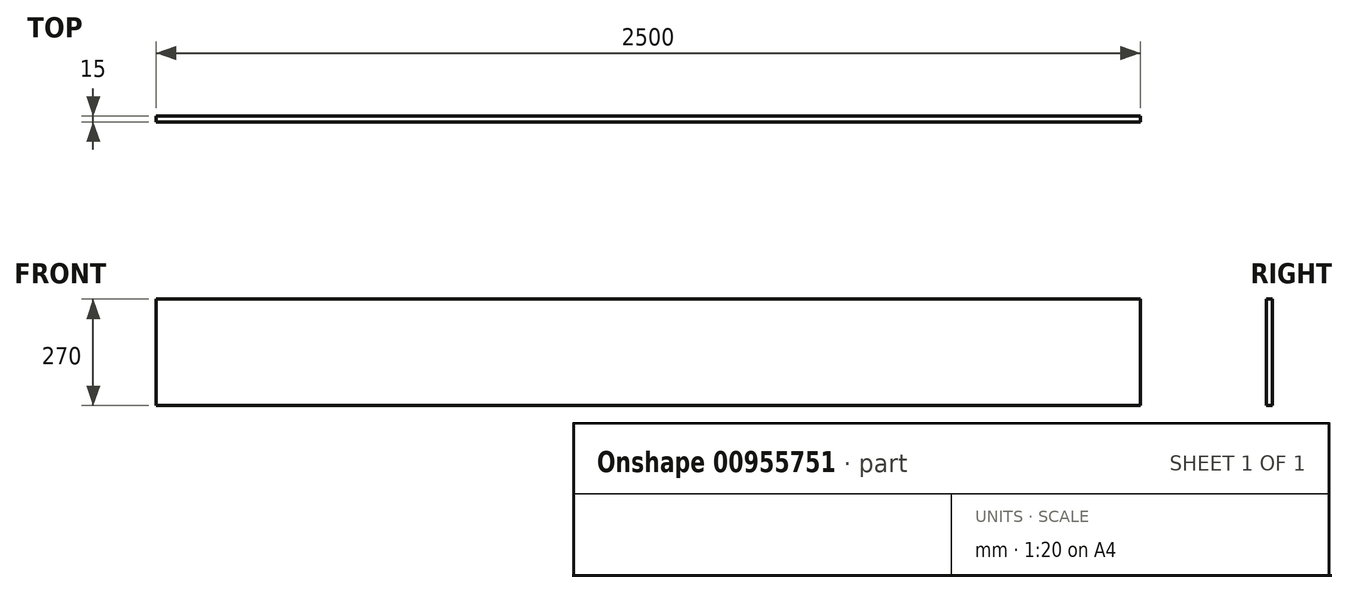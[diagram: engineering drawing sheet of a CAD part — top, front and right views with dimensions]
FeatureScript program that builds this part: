
annotation { "Feature Type Name" : "Feature", "Feature Type Description" : "" }
export const myFeature = defineFeature(function(context is Context, id is Id, definition is map)
    precondition{}
    {
        {
            var Q0;
            Q0=qCreatedBy(makeId("Front.planeOp"),FACE);
            var sketch = newSketch(context, id + "F0", { "sketchPlane" : qUnion([Q0])});
            skLineSegment(sketch, "E0.bottom", {"start": v(0, 0) * mm, "end": v(2500, 0) * mm});
            skLineSegment(sketch, "E0.top", {"start": v(0, -270) * mm, "end": v(2500, -270) * mm});
            skLineSegment(sketch, "E0.left", {"start": v(0, 0) * mm, "end": v(0, -270) * mm});
            skLineSegment(sketch, "E0.right", {"start": v(2500, 0) * mm, "end": v(2500, -270) * mm});
            skSolve(sketch);
        }
        {
            var Q0;
            Q0 = qSketchRegion(id + "F0", true);
            extrude(context, id + "F1", {"entities" : qUnion([Q0]), "depth" : 15 * mm, "offsetDistance" : 25 * mm});
        }
    });
